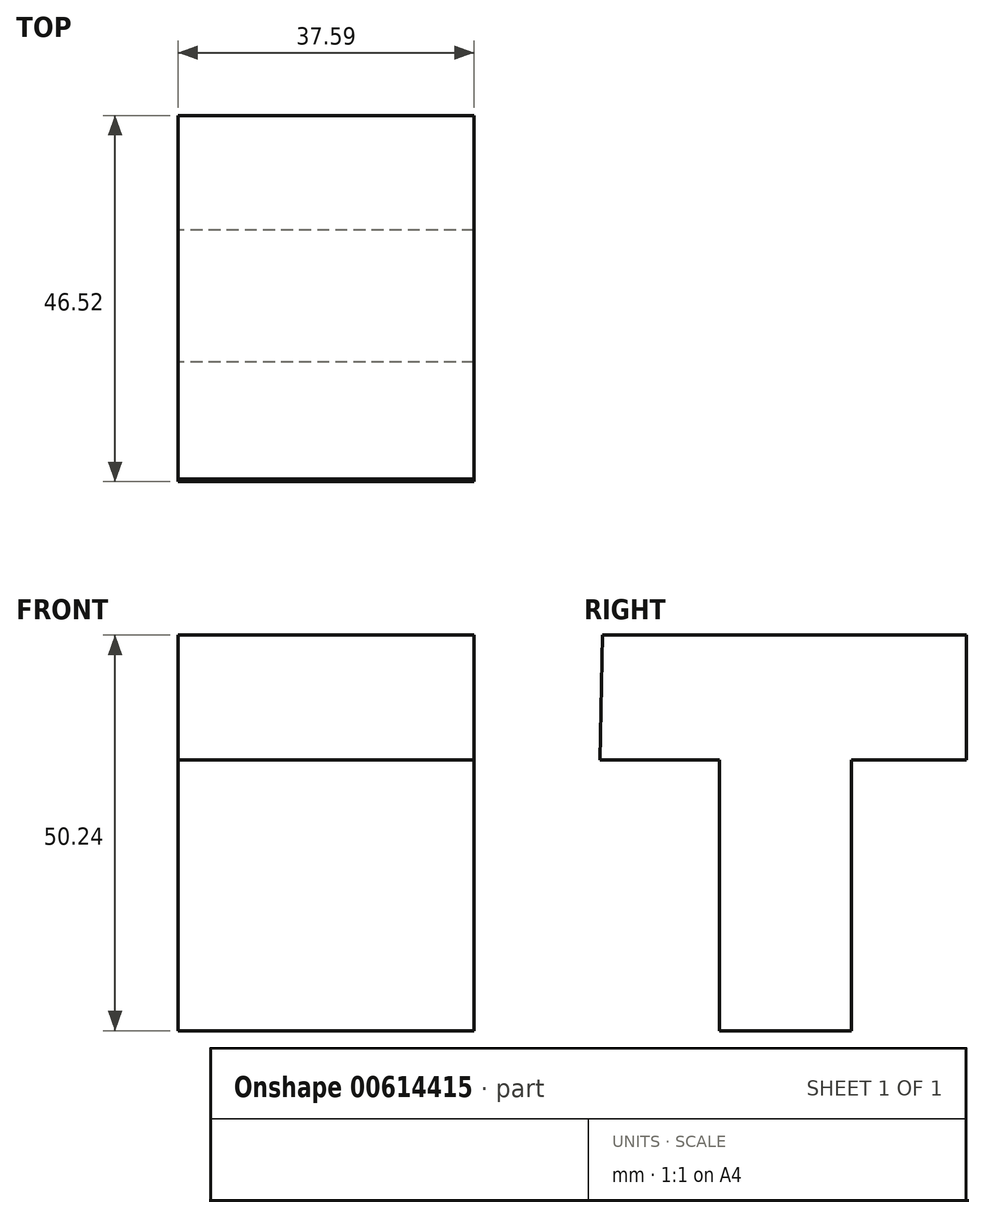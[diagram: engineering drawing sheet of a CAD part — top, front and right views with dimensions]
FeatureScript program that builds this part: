
annotation { "Feature Type Name" : "Feature", "Feature Type Description" : "" }
export const myFeature = defineFeature(function(context is Context, id is Id, definition is map)
    precondition{}
    {
        {
            var Q0;
            Q0=qCreatedBy(makeId("Right.planeOp"),FACE);
            var sketch = newSketch(context, id + "F0", { "sketchPlane" : qUnion([Q0])});
            skLineSegment(sketch, "E0", {"start": v(-62.18, 33.03) * mm, "end": v(-15.97, 33.03) * mm});
            skLineSegment(sketch, "E1", {"start": v(-15.97, 33.03) * mm, "end": v(-15.97, 17.21) * mm});
            skLineSegment(sketch, "E2", {"start": v(-15.97, 17.21) * mm, "end": v(-30.55, 17.21) * mm});
            skLineSegment(sketch, "E3", {"start": v(-30.55, 17.21) * mm, "end": v(-30.55, -17.21) * mm});
            skLineSegment(sketch, "E4", {"start": v(-30.55, -17.21) * mm, "end": v(-47.3, -17.21) * mm});
            skLineSegment(sketch, "E5", {"start": v(-47.3, -17.21) * mm, "end": v(-47.3, 17.21) * mm});
            skLineSegment(sketch, "E6", {"start": v(-47.3, 17.21) * mm, "end": v(-62.49, 17.21) * mm});
            skLineSegment(sketch, "E7", {"start": v(-62.49, 17.21) * mm, "end": v(-62.18, 33.03) * mm});
            skSolve(sketch);
        }
        {
            var Q0;
            Q0=makeQuery(id+"F0.imprint","IMPRINT",FACE,{"disambiguationData":[TD([[makeQuery(id+"F0.imprint","IMPRINT",EDGE,{"derivedFrom":sQuery(id+"F0.wireOp",EDGE,"E0")}),-1.0]])]});
            extrude(context, id + "F1", {"entities" : qUnion([Q0]), "depth" : 37.6 * mm, "offsetDistance" : 25.4 * mm});
        }
    });
